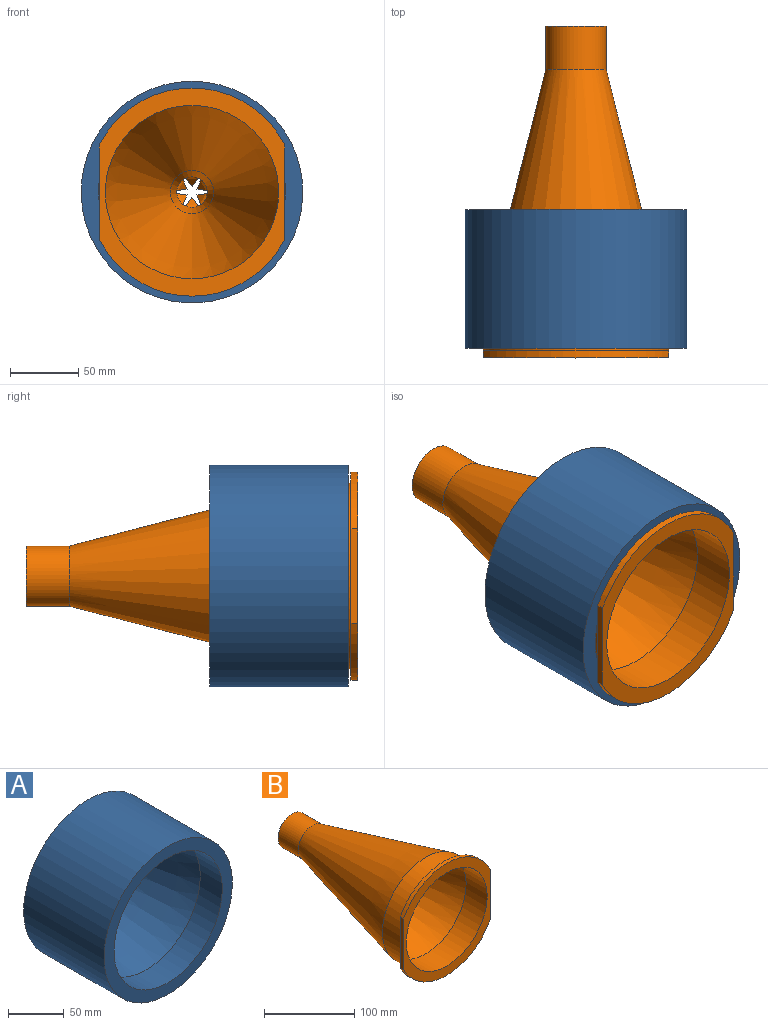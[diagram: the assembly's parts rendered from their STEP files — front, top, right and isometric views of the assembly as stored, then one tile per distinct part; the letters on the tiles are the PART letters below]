
ASSEMBLY  parts=2 mates=1
PART A: 6 faces, bbox 162.3x101.6x162.3 mm
  f0: cylinder r=50.42mm len=100.84mm, axis (0,1,0), area 2333.5mm2, adj f1,f5
  f1: plane 162.26x162.26mm, normal (0,1,0), area 12690.8mm2, adj f0,f2
  f2: cylinder r=81.13mm len=162.26mm, axis (0,1,0), area 51789.6mm2, adj f1,f3
  f3: plane 162.26x162.26mm, normal (0,-1,0), area 5967mm2, adj f2,f4
  f4: cylinder r=68.43mm len=136.86mm, axis (0,1,0), area 12012.6mm2, adj f3,f5
  f5: cone r=68.43mm half-angle=15.2deg, axis (0,-1,0), area 25649mm2, adj f0,f4
PART B: 38 faces, bbox 135.9x242.9x152.4 mm
  f0: cone r=2.54mm half-angle=37.8deg, axis (0,-1,0), area 57mm2, adj f18,f20,f21,f22,f37
  f1: cone r=2.54mm half-angle=37.8deg, axis (0,-1,0), area 57mm2, adj f18,f34,f35,f36,f37
  f2: cone r=2.54mm half-angle=37.8deg, axis (0,-1,0), area 57mm2, adj f18,f31,f32,f33,f34
  f3: cone r=2.54mm half-angle=37.8deg, axis (0,-1,0), area 57mm2, adj f18,f28,f29,f30,f31
  f4: cone r=2.54mm half-angle=37.8deg, axis (0,-1,0), area 56.3mm2, adj f18,f25,f26,f27,f28
  f5: cone r=2.54mm half-angle=37.8deg, axis (0,-1,0), area 57.7mm2, adj f18,f22,f23,f24,f25
  f6: plane 135.89x76.2mm, normal (0,1,0), area 1485.1mm2, adj f9,f13,f15,f16
  f7: plane 135.89x76.2mm, normal (0,1,0), area 1485.1mm2, adj f13,f14,f15,f16
  f8: plane 152.4x135.89mm, normal (0,-1,0), area 4805.8mm2, adj f9,f12,f14,f15,f16
  f9: cylinder r=76.2mm len=135.89mm, axis (0,1,0), area 852.4mm2, adj f6,f8,f15,f16
  f10: cone r=22.02mm half-angle=14.5deg, axis (0,-1,0), area 51999.7mm2, adj f13,f17
  f11: cone r=63.5mm half-angle=15deg, axis (0,-1,0), area 45985.5mm2, adj f12,f18
  f12: cylinder r=63.5mm len=127mm, axis (0,1,0), area 13174.4mm2, adj f8,f11
  f13: cylinder r=67.95mm len=135.89mm, axis (0,1,0), area 11927.9mm2, adj f6,f7,f10
  f14: cylinder r=76.2mm len=135.89mm, axis (0,1,0), area 852.4mm2, adj f7,f8,f15,f16
  f15: plane 68.99x5.08mm, normal (-1,0,0), area 350.5mm2, adj f6,f7,f8,f9,f14
  f16: plane 68.99x5.08mm, normal (1,0,0), area 350.5mm2, adj f6,f7,f8,f9,f14
  f17: cylinder r=22.02mm len=44.04mm, axis (0,-1,0), area 4393.2mm2, adj f10,f19
  f18: cone r=15.88mm half-angle=12.7deg, axis (0,-1,0), area 1789.8mm2, adj f0,f1,f2,f3,f4,f5,f11
  f19: plane 44.04x44.04mm, normal (0,1,0), area 1333.5mm2, adj f17,f20,f21,f22,f23,f24,f25,f26
  f20: plane 9.95x6.54mm, normal (-0.13,0,0.99), area 39.1mm2, adj f0,f19,f21,f37
  f21: plane 9.95x6.08mm, normal (-0.92,0,-0.39), area 39.1mm2, adj f0,f19,f20,f22
  f22: cylinder r=1.27mm len=11.28mm, axis (0,1,0), area 38.9mm2, adj f0,f5,f19,f21,f23
  f23: plane 9.95x5.27mm, normal (0.8,0,0.61), area 39.2mm2, adj f5,f19,f22,f24
  f24: plane 9.95x5.24mm, normal (-0.79,0,0.61), area 39.2mm2, adj f5,f19,f23,f25
  f25: cylinder r=1.27mm len=11.28mm, axis (0,1,0), area 38.9mm2, adj f4,f5,f19,f24,f26
  f26: plane 9.95x6.04mm, normal (0.92,0,-0.39), area 39.1mm2, adj f4,f19,f25,f27
  f27: plane 9.95x6.51mm, normal (0.13,0,0.99), area 39.1mm2, adj f4,f19,f26,f28
  f28: cylinder r=1.27mm len=11.28mm, axis (0,1,0), area 38.9mm2, adj f3,f4,f19,f27,f29
  f29: plane 9.95x6.54mm, normal (0.13,0,-0.99), area 39.1mm2, adj f3,f19,f28,f30
  f30: plane 9.95x6.08mm, normal (0.92,0,0.39), area 39.1mm2, adj f3,f19,f29,f31
  f31: cylinder r=1.27mm len=11.28mm, axis (0,1,0), area 38.9mm2, adj f2,f3,f19,f30,f32
  f32: plane 9.95x5.25mm, normal (-0.8,0,-0.61), area 39.1mm2, adj f2,f19,f31,f33
  f33: plane 9.95x5.25mm, normal (0.8,0,-0.61), area 39.1mm2, adj f2,f19,f32,f34
  f34: cylinder r=1.27mm len=11.28mm, axis (0,1,0), area 38.9mm2, adj f1,f2,f19,f33,f35
  f35: plane 9.95x6.08mm, normal (-0.92,0,0.39), area 39.1mm2, adj f1,f19,f34,f36
  f36: plane 9.95x6.54mm, normal (-0.13,0,-0.99), area 39.1mm2, adj f1,f19,f35,f37
  f37: cylinder r=1.27mm len=11.28mm, axis (0,1,0), area 38.9mm2, adj f0,f1,f19,f20,f36
PLACE A t=(0,-102.69,0)mm
PLACE B at identity fixed
MATE slider B.f13 <-> A.f0  axis (0,1,0) through (0,-192.13,0)mm
